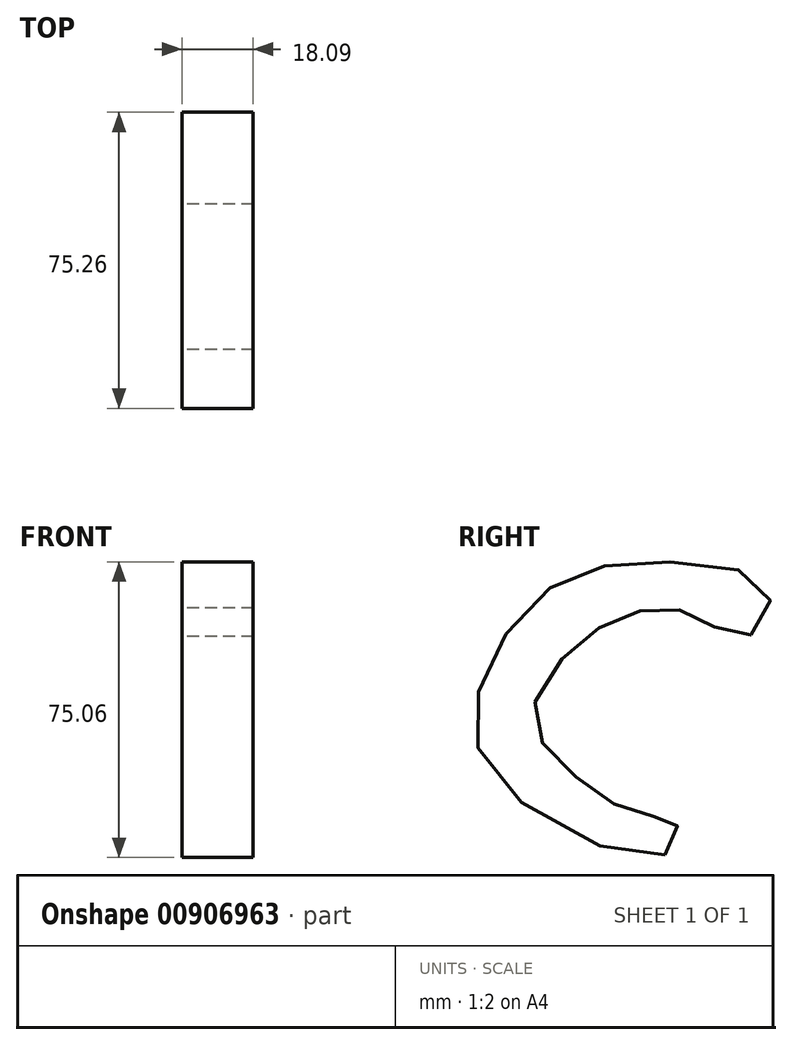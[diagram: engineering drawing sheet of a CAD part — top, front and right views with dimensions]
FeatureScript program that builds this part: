
annotation { "Feature Type Name" : "Feature", "Feature Type Description" : "" }
export const myFeature = defineFeature(function(context is Context, id is Id, definition is map)
    precondition{}
    {
        {
            var Q0;
            Q0=qCreatedBy(makeId("Right.planeOp"),FACE);
            var sketch = newSketch(context, id + "F0", { "sketchPlane" : qUnion([Q0])});
            skFitSpline(sketch, "E0", {"points": [v(11.38, -42.53) * mm, v(-30.28, -24.55) * mm, v(-35.59, 0) * mm, v(-17.65, 25.38) * mm, v(10.55, 31.87) * mm, v(37.4, 25.03) * mm, v(33.92, 13.62) * mm, v(23.7, 15.46) * mm, v(13.1, 20.06) * mm, v(0, 17.7) * mm, v(-13.78, 8.28) * mm, v(-22.17, -7.93) * mm, v(-13.77, -20.54) * mm, v(0, -30.33) * mm, v(11.35, -33.33) * mm, v(14.6, -35.31) * mm, v(11.38, -42.53) * mm]});
            skSolve(sketch);
        }
        {
            var Q0;
            Q0 = qSketchRegion(id + "F0", true);
            extrude(context, id + "F1", {"entities" : qUnion([Q0]), "depth" : 18.1 * mm, "offsetDistance" : 25.4 * mm});
        }
    });
